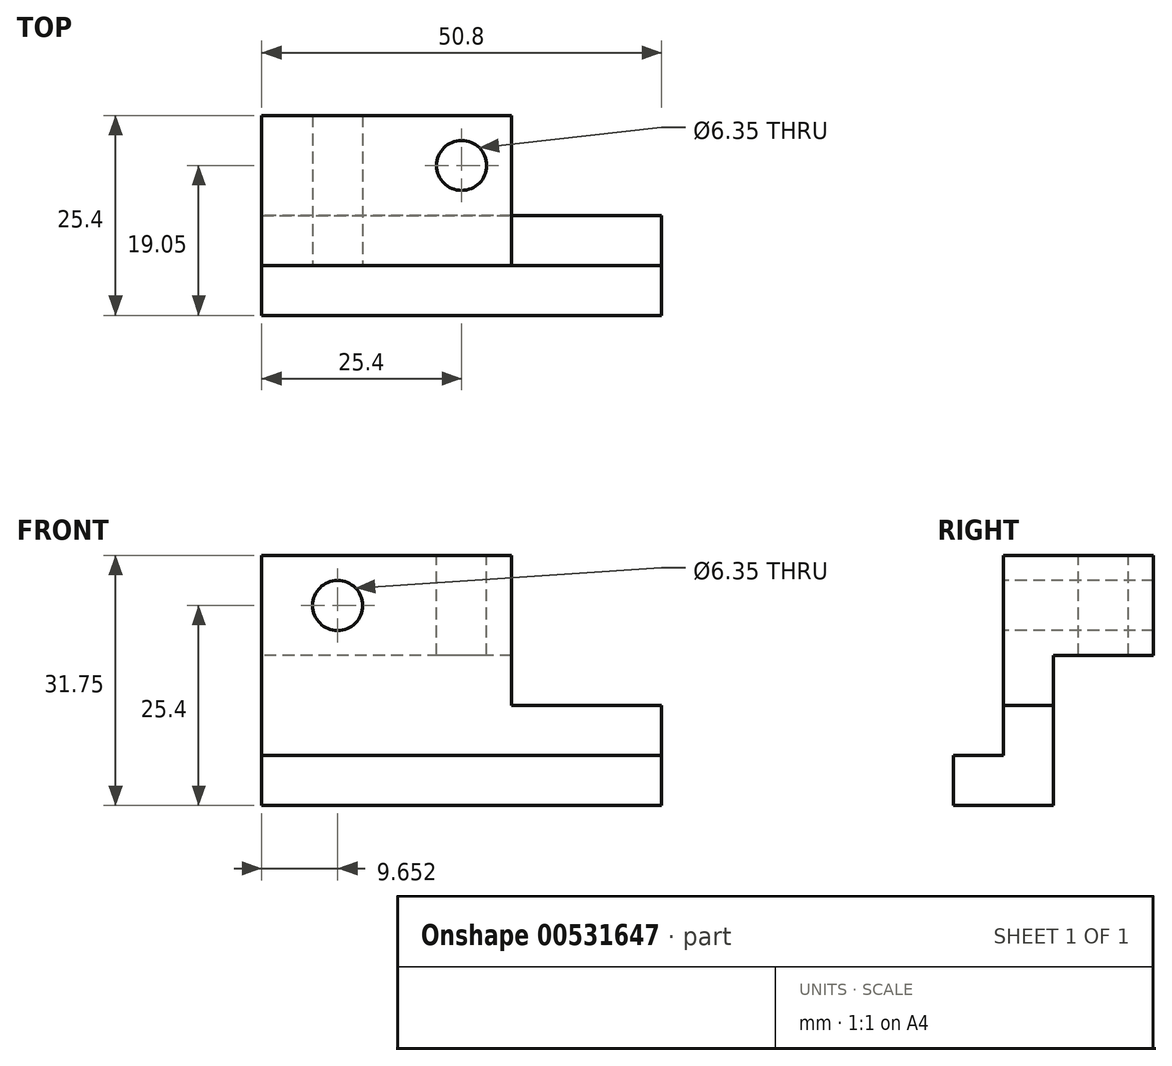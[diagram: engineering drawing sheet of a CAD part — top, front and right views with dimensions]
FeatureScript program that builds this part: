
annotation { "Feature Type Name" : "Feature", "Feature Type Description" : "" }
export const myFeature = defineFeature(function(context is Context, id is Id, definition is map)
    precondition{}
    {
        {
            var Q0;
            Q0=qCreatedBy(makeId("Front.planeOp"),FACE);
            var sketch = newSketch(context, id + "F0", { "sketchPlane" : qUnion([Q0])});
            skLineSegment(sketch, "E0", {"start": v(0, 0) * mm, "end": v(0, 19.05) * mm});
            skLineSegment(sketch, "E1", {"start": v(0, 19.05) * mm, "end": v(-31.75, 19.05) * mm});
            skLineSegment(sketch, "E2", {"start": v(-31.75, 19.05) * mm, "end": v(-31.75, -6.35) * mm});
            skLineSegment(sketch, "E3", {"start": v(-31.75, -6.35) * mm, "end": v(19.05, -6.35) * mm});
            skLineSegment(sketch, "E4", {"start": v(19.05, -6.35) * mm, "end": v(19.05, 0) * mm});
            skLineSegment(sketch, "E5", {"start": v(19.05, 0) * mm, "end": v(0, 0) * mm});
            skSolve(sketch);
        }
        {
            var Q0;
            Q0 = qSketchRegion(id + "F0", true);
            extrude(context, id + "F1", {"entities" : qUnion([Q0]), "depth" : 6.35 * mm, "offsetDistance" : 25.4 * mm});
        }
        {
            var Q0;
            Q0=qCreatedBy(makeId("Front.planeOp"),FACE);
            var sketch = newSketch(context, id + "F2", { "sketchPlane" : qUnion([Q0])});
            skLineSegment(sketch, "E6.bottom", {"start": v(-31.75, -6.35) * mm, "end": v(19.05, -6.35) * mm});
            skLineSegment(sketch, "E6.top", {"start": v(-31.75, -12.7) * mm, "end": v(19.05, -12.7) * mm});
            skLineSegment(sketch, "E6.left", {"start": v(-31.75, -6.35) * mm, "end": v(-31.75, -12.7) * mm});
            skLineSegment(sketch, "E6.right", {"start": v(19.05, -6.35) * mm, "end": v(19.05, -12.7) * mm});
            skSolve(sketch);
        }
        {
            var Q0;
            Q0 = qSketchRegion(id + "F2", true);
            extrude(context, id + "F3", {"entities" : qUnion([Q0]), "operationType" : NewBodyOperationType.ADD, "depth" : 12.7 * mm, "offsetDistance" : 25.4 * mm});
        }
        {
            var Q0;
            Q0=makeQuery(id+"F3.boolean.opBoolean","MERGE",FACE,{"derivedFrom":[makeQuery(id+"F1.opExtrude","CAP_FACE",FACE,{"disambiguationData":[OSD([sQuery(id+"F0.wireOp",EDGE,"E0"),sQuery(id+"F0.wireOp",EDGE,"E1"),sQuery(id+"F0.wireOp",EDGE,"E2"),sQuery(id+"F0.wireOp",EDGE,"E3"),sQuery(id+"F0.wireOp",EDGE,"E4"),sQuery(id+"F0.wireOp",EDGE,"E5")])],"isStart":true}),makeQuery(id+"F3.opExtrude","CAP_FACE",FACE,{"disambiguationData":[OSD([sQuery(id+"F2.wireOp",EDGE,"E6.bottom"),sQuery(id+"F2.wireOp",EDGE,"E6.top"),sQuery(id+"F2.wireOp",EDGE,"E6.left"),sQuery(id+"F2.wireOp",EDGE,"E6.right")])],"isStart":true})]});
            var sketch = newSketch(context, id + "F4", { "sketchPlane" : qUnion([Q0])});
            skLineSegment(sketch, "E7.bottom", {"start": v(0, 19.05) * mm, "end": v(31.75, 19.05) * mm});
            skLineSegment(sketch, "E7.top", {"start": v(0, 6.35) * mm, "end": v(31.75, 6.35) * mm});
            skLineSegment(sketch, "E7.left", {"start": v(0, 19.05) * mm, "end": v(0, 6.35) * mm});
            skLineSegment(sketch, "E7.right", {"start": v(31.75, 19.05) * mm, "end": v(31.75, 6.35) * mm});
            skSolve(sketch);
        }
        {
            var Q0;
            Q0 = qSketchRegion(id + "F4", true);
            extrude(context, id + "F5", {"entities" : qUnion([Q0]), "operationType" : NewBodyOperationType.ADD, "depth" : 12.7 * mm, "offsetDistance" : 25.4 * mm});
        }
        {
            var Q0;
            Q0=makeQuery(id+"F1.opExtrude","CAP_FACE",FACE,{"disambiguationData":[OSD([sQuery(id+"F0.wireOp",EDGE,"E0"),sQuery(id+"F0.wireOp",EDGE,"E1"),sQuery(id+"F0.wireOp",EDGE,"E2"),sQuery(id+"F0.wireOp",EDGE,"E3"),sQuery(id+"F0.wireOp",EDGE,"E4"),sQuery(id+"F0.wireOp",EDGE,"E5")])],"isStart":false});
            var sketch = newSketch(context, id + "F6", { "sketchPlane" : qUnion([Q0])});
            skCircle(sketch, "E8", {"center": v(-22.1, 12.7) * mm, "radius": 3.18 * mm});
            skSolve(sketch);
        }
        {
            var Q0;
            Q0 = qSketchRegion(id + "F6", true);
            extrude(context, id + "F7", {"entities" : qUnion([Q0]), "operationType" : NewBodyOperationType.REMOVE, "oppositeDirection" : true, "depth" : 25.4 * mm, "offsetDistance" : 25.4 * mm});
        }
        {
            var Q0;
            Q0=makeQuery(id+"F5.boolean.opBoolean","MERGE",FACE,{"derivedFrom":[makeQuery(id+"F1.opExtrude","SWEPT_FACE",FACE,{"disambiguationData":[OSD([sQuery(id+"F0.wireOp",EDGE,"E1")])]}),makeQuery(id+"F5.opExtrude","SWEPT_FACE",FACE,{"disambiguationData":[OSD([sQuery(id+"F4.wireOp",EDGE,"E7.bottom")])]})]});
            var sketch = newSketch(context, id + "F8", { "sketchPlane" : qUnion([Q0])});
            skCircle(sketch, "E9", {"center": v(-6.35, 6.35) * mm, "radius": 3.18 * mm});
            skSolve(sketch);
        }
        {
            var Q0;
            Q0 = qSketchRegion(id + "F8", true);
            extrude(context, id + "F9", {"entities" : qUnion([Q0]), "operationType" : NewBodyOperationType.REMOVE, "oppositeDirection" : true, "depth" : 25.4 * mm, "offsetDistance" : 25.4 * mm});
        }
    });
